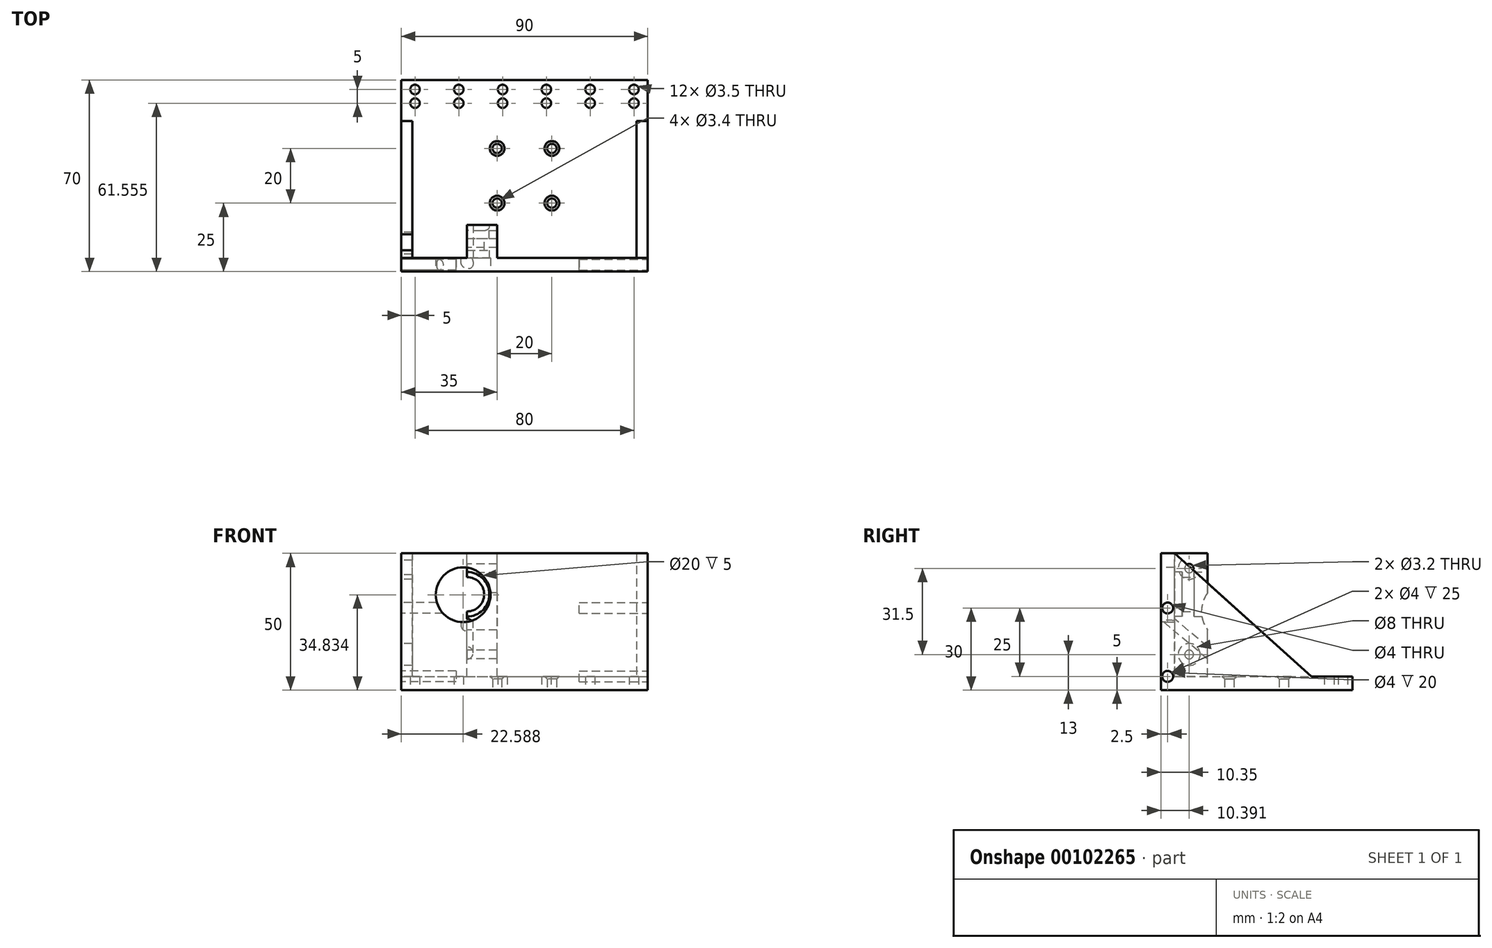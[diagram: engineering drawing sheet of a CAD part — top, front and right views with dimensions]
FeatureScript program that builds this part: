
annotation { "Feature Type Name" : "Feature", "Feature Type Description" : "" }
export const myFeature = defineFeature(function(context is Context, id is Id, definition is map)
    precondition{}
    {
        {
            var Q0;
            Q0=qCreatedBy(makeId("Top.planeOp"),FACE);
            var sketch = newSketch(context, id + "F0", { "sketchPlane" : qUnion([Q0])});
            skLineSegment(sketch, "E0.bottom", {"start": v(0, 0) * mm, "end": v(90, 0) * mm});
            skLineSegment(sketch, "E0.top", {"start": v(0, 70) * mm, "end": v(90, 70) * mm});
            skLineSegment(sketch, "E0.right", {"start": v(90, 0) * mm, "end": v(90, 70) * mm});
            skLineSegment(sketch, "E1", {"start": v(0, 35) * mm, "end": v(98.43, 35) * mm, "construction": true});
            skPoint(sketch, "E1.endSnap0", {"position": v(90, 35) * mm});
            skLineSegment(sketch, "E2", {"start": v(45, 70) * mm, "end": v(45, -10.85) * mm, "construction": true});
            skCircle(sketch, "E3", {"center": v(55, 45) * mm, "radius": 1.7 * mm});
            skCircle(sketch, "E4", {"center": v(55, 25) * mm, "radius": 1.7 * mm});
            skCircle(sketch, "E5", {"center": v(35, 45) * mm, "radius": 1.7 * mm});
            skCircle(sketch, "E6", {"center": v(35, 25) * mm, "radius": 1.7 * mm});
            skCircle(sketch, "E7", {"center": v(5, 66.55) * mm, "radius": 1.75 * mm});
            skCircle(sketch, "E8", {"center": v(5, 61.55) * mm, "radius": 1.75 * mm});
            skCircle(sketch, "E9.1.0.0", {"center": v(21, 66.55) * mm, "radius": 1.75 * mm});
            skCircle(sketch, "E9.1.0.1", {"center": v(21, 61.55) * mm, "radius": 1.75 * mm});
            skCircle(sketch, "E9.2.0.0", {"center": v(37, 66.55) * mm, "radius": 1.75 * mm});
            skCircle(sketch, "E9.2.0.1", {"center": v(37, 61.55) * mm, "radius": 1.75 * mm});
            skCircle(sketch, "E9.3.0.0", {"center": v(53, 66.55) * mm, "radius": 1.75 * mm});
            skCircle(sketch, "E9.3.0.1", {"center": v(53, 61.55) * mm, "radius": 1.75 * mm});
            skCircle(sketch, "E9.4.0.0", {"center": v(69, 66.55) * mm, "radius": 1.75 * mm});
            skCircle(sketch, "E9.4.0.1", {"center": v(69, 61.55) * mm, "radius": 1.75 * mm});
            skCircle(sketch, "E9.5.0.0", {"center": v(85, 66.55) * mm, "radius": 1.75 * mm});
            skCircle(sketch, "E9.5.0.1", {"center": v(85, 61.55) * mm, "radius": 1.75 * mm});
            skLineSegment(sketch, "E9.direction1", {"start": v(5, 66.55) * mm, "end": v(21, 66.55) * mm, "construction": true});
            skLineSegment(sketch, "E10", {"start": v(0, 70) * mm, "end": v(0, 0) * mm});
            skSolve(sketch);
        }
        {
            var Q0;
            Q0 = qSketchRegion(id + "F0", true);
            extrude(context, id + "F1", {"entities" : qUnion([Q0]), "depth" : 5 * mm});
        }
        {
            var Q0;
            Q0=makeQuery(id+"F1.opExtrude","CAP_FACE",FACE,{"disambiguationData":[OSD([sQuery(id+"F0.wireOp",EDGE,"E0.bottom"),sQuery(id+"F0.wireOp",EDGE,"E0.top"),sQuery(id+"F0.wireOp",EDGE,"E0.right"),sQuery(id+"F0.wireOp",EDGE,"E3"),sQuery(id+"F0.wireOp",EDGE,"E4"),sQuery(id+"F0.wireOp",EDGE,"E5"),sQuery(id+"F0.wireOp",EDGE,"E6"),sQuery(id+"F0.wireOp",EDGE,"E7"),sQuery(id+"F0.wireOp",EDGE,"E8"),sQuery(id+"F0.wireOp",EDGE,"E9.1.0.0"),sQuery(id+"F0.wireOp",EDGE,"E9.1.0.1"),sQuery(id+"F0.wireOp",EDGE,"E9.2.0.0"),sQuery(id+"F0.wireOp",EDGE,"E9.2.0.1"),sQuery(id+"F0.wireOp",EDGE,"E9.3.0.0"),sQuery(id+"F0.wireOp",EDGE,"E9.3.0.1"),sQuery(id+"F0.wireOp",EDGE,"E9.4.0.0"),sQuery(id+"F0.wireOp",EDGE,"E9.4.0.1"),sQuery(id+"F0.wireOp",EDGE,"E9.5.0.0"),sQuery(id+"F0.wireOp",EDGE,"E9.5.0.1"),sQuery(id+"F0.wireOp",EDGE,"E10")])],"isStart":false});
            var sketch = newSketch(context, id + "F2", { "sketchPlane" : qUnion([Q0])});
            skLineSegment(sketch, "E11.bottom", {"start": v(0, 0) * mm, "end": v(90, 0) * mm});
            skLineSegment(sketch, "E11.top", {"start": v(0, 5) * mm, "end": v(90, 5) * mm});
            skLineSegment(sketch, "E11.left", {"start": v(0, 0) * mm, "end": v(0, 5) * mm});
            skLineSegment(sketch, "E11.right", {"start": v(90, 0) * mm, "end": v(90, 5) * mm});
            skSolve(sketch);
        }
        {
            var Q0;
            Q0 = qSketchRegion(id + "F2", true);
            extrude(context, id + "F3", {"entities" : qUnion([Q0]), "operationType" : NewBodyOperationType.ADD, "depth" : 45 * mm});
        }
        {
            var Q0;
            Q0=makeQuery(id+"F3.opExtrude","SWEPT_FACE",FACE,{"disambiguationData":[OSD([sQuery(id+"F2.wireOp",EDGE,"E11.top")])]});
            var sketch = newSketch(context, id + "F4", { "sketchPlane" : qUnion([Q0])});
            skLineSegment(sketch, "E12.bottom", {"start": v(-35, 5) * mm, "end": v(-24, 5) * mm});
            skLineSegment(sketch, "E12.top", {"start": v(-35, 50) * mm, "end": v(-24, 50) * mm});
            skLineSegment(sketch, "E12.left", {"start": v(-35, 5) * mm, "end": v(-35, 50) * mm});
            skLineSegment(sketch, "E12.right", {"start": v(-24, 5) * mm, "end": v(-24, 50) * mm});
            skSolve(sketch);
        }
        {
            var Q0;
            Q0 = qSketchRegion(id + "F4", true);
            extrude(context, id + "F5", {"entities" : qUnion([Q0]), "operationType" : NewBodyOperationType.ADD, "depth" : 12.1 * mm});
        }
        {
            var Q0;
            Q0=makeQuery(id+"F5.opExtrude","CAP_FACE",FACE,{"disambiguationData":[OSD([sQuery(id+"F4.wireOp",EDGE,"E12.bottom"),sQuery(id+"F4.wireOp",EDGE,"E12.top"),sQuery(id+"F4.wireOp",EDGE,"E12.left"),sQuery(id+"F4.wireOp",EDGE,"E12.right")])],"isStart":false});
            var sketch = newSketch(context, id + "F6", { "sketchPlane" : qUnion([Q0])});
            skCircle(sketch, "E13", {"center": v(-24, 35) * mm, "radius": 6.25 * mm});
            skSolve(sketch);
        }
        {
            var Q0;
            Q0 = qSketchRegion(id + "F6", true);
            extrude(context, id + "F7", {"entities" : qUnion([Q0]), "operationType" : NewBodyOperationType.REMOVE, "oppositeDirection" : true, "depth" : 25 * mm});
        }
        {
            var Q0;
            Q0=makeQuery(id+"F5.opExtrude","CAP_FACE",FACE,{"disambiguationData":[OSD([sQuery(id+"F4.wireOp",EDGE,"E12.bottom"),sQuery(id+"F4.wireOp",EDGE,"E12.top"),sQuery(id+"F4.wireOp",EDGE,"E12.left"),sQuery(id+"F4.wireOp",EDGE,"E12.right")])],"isStart":false});
            var sketch = newSketch(context, id + "F8", { "sketchPlane" : qUnion([Q0])});
            skCircle(sketch, "E14", {"center": v(-24, 35) * mm, "radius": 8.15 * mm});
            skSolve(sketch);
        }
        {
            var Q0;
            Q0 = qSketchRegion(id + "F8", true);
            extrude(context, id + "F9", {"entities" : qUnion([Q0]), "operationType" : NewBodyOperationType.REMOVE, "oppositeDirection" : true, "depth" : 5 * mm});
        }
        {
            var Q0;
            Q0=makeQuery(id+"F3.boolean.opBoolean","MERGE",FACE,{"derivedFrom":[makeQuery(id+"F1.opExtrude","SWEPT_FACE",FACE,{"disambiguationData":[OSD([sQuery(id+"F0.wireOp",EDGE,"E0.bottom")])]}),makeQuery(id+"F3.opExtrude","SWEPT_FACE",FACE,{"disambiguationData":[OSD([sQuery(id+"F2.wireOp",EDGE,"E11.bottom")])]})]});
            var sketch = newSketch(context, id + "F10", { "sketchPlane" : qUnion([Q0])});
            skCircle(sketch, "E15", {"center": v(22.59, 34.83) * mm, "radius": 10 * mm});
            skSolve(sketch);
        }
        {
            var Q0;
            Q0 = qSketchRegion(id + "F10", true);
            extrude(context, id + "F11", {"entities" : qUnion([Q0]), "operationType" : NewBodyOperationType.REMOVE, "oppositeDirection" : true, "depth" : 5 * mm});
        }
        {
            var Q0;
            Q0=makeQuery(id+"F11.boolean.opBoolean","COPY",FACE,{"derivedFrom":makeQuery(id+"F11.opExtrude","CAP_FACE",FACE,{"disambiguationData":[OSD([sQuery(id+"F10.wireOp",EDGE,"E15")])],"isStart":false})});
            var sketch = newSketch(context, id + "F12", { "sketchPlane" : qUnion([Q0])});
            skCircle(sketch, "E16", {"center": v(24, 35) * mm, "radius": 8.15 * mm});
            skSolve(sketch);
        }
        {
            var Q0;
            Q0 = qSketchRegion(id + "F12", true);
            extrude(context, id + "F13", {"entities" : qUnion([Q0]), "operationType" : NewBodyOperationType.REMOVE, "oppositeDirection" : true, "depth" : 2.8 * mm});
        }
        {
            var Q0;
            {var subQ0=sQuery(id+"F4.wireOp",EDGE,"E12.right");Q0=makeQuery(id+"F7.boolean.opBoolean","SPLIT",FACE,{"disambiguationData":[TD([makeQuery(id+"F1.opExtrude","CAP_FACE",FACE,{"disambiguationData":[OSD([sQuery(id+"F0.wireOp",EDGE,"E0.bottom"),sQuery(id+"F0.wireOp",EDGE,"E0.top"),sQuery(id+"F0.wireOp",EDGE,"E0.right"),sQuery(id+"F0.wireOp",EDGE,"E3"),sQuery(id+"F0.wireOp",EDGE,"E4"),sQuery(id+"F0.wireOp",EDGE,"E5"),sQuery(id+"F0.wireOp",EDGE,"E6"),sQuery(id+"F0.wireOp",EDGE,"E7"),sQuery(id+"F0.wireOp",EDGE,"E8"),sQuery(id+"F0.wireOp",EDGE,"E9.1.0.0"),sQuery(id+"F0.wireOp",EDGE,"E9.1.0.1"),sQuery(id+"F0.wireOp",EDGE,"E9.2.0.0"),sQuery(id+"F0.wireOp",EDGE,"E9.2.0.1"),sQuery(id+"F0.wireOp",EDGE,"E9.3.0.0"),sQuery(id+"F0.wireOp",EDGE,"E9.3.0.1"),sQuery(id+"F0.wireOp",EDGE,"E9.4.0.0"),sQuery(id+"F0.wireOp",EDGE,"E9.4.0.1"),sQuery(id+"F0.wireOp",EDGE,"E9.5.0.0"),sQuery(id+"F0.wireOp",EDGE,"E9.5.0.1"),sQuery(id+"F0.wireOp",EDGE,"E10")])],"isStart":false})])],"derivedFrom":makeQuery(id+"F5.opExtrude","SWEPT_FACE",FACE,{"disambiguationData":[OSD([subQ0])]})});}
            var sketch = newSketch(context, id + "F14", { "sketchPlane" : qUnion([Q0])});
            skCircle(sketch, "E17", {"center": v(-10.35, 44.5) * mm, "radius": 1.6 * mm});
            skCircle(sketch, "E18", {"center": v(-10.35, 13) * mm, "radius": 1.6 * mm});
            skCircle(sketch, "E19", {"center": v(-26.1, 28.75) * mm, "radius": 11.25 * mm});
            skSolve(sketch);
        }
        {
            var Q0;
            Q0 = qSketchRegion(id + "F14", true);
            extrude(context, id + "F15", {"entities" : qUnion([Q0]), "operationType" : NewBodyOperationType.REMOVE, "oppositeDirection" : true, "depth" : 25 * mm});
        }
        {
            var Q0;
            Q0=makeQuery(id+"F3.boolean.opBoolean","MERGE",FACE,{"derivedFrom":[makeQuery(id+"F1.opExtrude","SWEPT_FACE",FACE,{"disambiguationData":[OSD([sQuery(id+"F0.wireOp",EDGE,"E10")])]}),makeQuery(id+"F3.opExtrude","SWEPT_FACE",FACE,{"disambiguationData":[OSD([sQuery(id+"F2.wireOp",EDGE,"E11.left")])]})]});
            var sketch = newSketch(context, id + "F16", { "sketchPlane" : qUnion([Q0])});
            skLineSegment(sketch, "E20", {"start": v(-5, 50) * mm, "end": v(-55, 5) * mm});
            skLineSegment(sketch, "E21", {"start": v(-55, 5) * mm, "end": v(-55, 0) * mm});
            skLineSegment(sketch, "E22", {"start": v(-55, 0) * mm, "end": v(0, 0) * mm});
            skLineSegment(sketch, "E23", {"start": v(0, 0) * mm, "end": v(0, 50) * mm});
            skLineSegment(sketch, "E24", {"start": v(0, 50) * mm, "end": v(-5, 50) * mm});
            skSolve(sketch);
        }
        {
            var Q0;
            Q0 = qSketchRegion(id + "F16", true);
            extrude(context, id + "F17", {"entities" : qUnion([Q0]), "operationType" : NewBodyOperationType.ADD, "oppositeDirection" : true, "depth" : 4 * mm});
        }
        {
            var Q0;
            Q0=makeQuery(id+"F3.boolean.opBoolean","MERGE",FACE,{"derivedFrom":[makeQuery(id+"F1.opExtrude","SWEPT_FACE",FACE,{"disambiguationData":[OSD([sQuery(id+"F0.wireOp",EDGE,"E0.right")])]}),makeQuery(id+"F3.opExtrude","SWEPT_FACE",FACE,{"disambiguationData":[OSD([sQuery(id+"F2.wireOp",EDGE,"E11.right")])]})]});
            var sketch = newSketch(context, id + "F18", { "sketchPlane" : qUnion([Q0])});
            skLineSegment(sketch, "E25", {"start": v(5, 50) * mm, "end": v(55, 5) * mm});
            skLineSegment(sketch, "E26", {"start": v(55, 5) * mm, "end": v(55, 0) * mm});
            skLineSegment(sketch, "E27", {"start": v(55, 0) * mm, "end": v(0, 0) * mm});
            skLineSegment(sketch, "E28", {"start": v(0, 0) * mm, "end": v(0, 50) * mm});
            skLineSegment(sketch, "E29", {"start": v(0, 50) * mm, "end": v(5, 50) * mm});
            skSolve(sketch);
        }
        {
            var Q0;
            Q0 = qSketchRegion(id + "F18", true);
            extrude(context, id + "F19", {"entities" : qUnion([Q0]), "operationType" : NewBodyOperationType.ADD, "oppositeDirection" : true, "depth" : 4 * mm});
        }
        {
            var Q0;
            Q0=makeQuery(id+"F17.boolean.opBoolean","MERGE",FACE,{"derivedFrom":[makeQuery(id+"F3.boolean.opBoolean","MERGE",FACE,{"derivedFrom":[makeQuery(id+"F1.opExtrude","SWEPT_FACE",FACE,{"disambiguationData":[OSD([sQuery(id+"F0.wireOp",EDGE,"E10")])]}),makeQuery(id+"F3.opExtrude","SWEPT_FACE",FACE,{"disambiguationData":[OSD([sQuery(id+"F2.wireOp",EDGE,"E11.left")])]})]}),makeQuery(id+"F17.opExtrude","CAP_FACE",FACE,{"disambiguationData":[OSD([sQuery(id+"F16.wireOp",EDGE,"E20"),sQuery(id+"F16.wireOp",EDGE,"E21"),sQuery(id+"F16.wireOp",EDGE,"E22"),sQuery(id+"F16.wireOp",EDGE,"E23"),sQuery(id+"F16.wireOp",EDGE,"E24")])],"isStart":true})]});
            var sketch = newSketch(context, id + "F20", { "sketchPlane" : qUnion([Q0])});
            skCircle(sketch, "E30", {"center": v(-10.4, 44.5) * mm, "radius": 4 * mm});
            skCircle(sketch, "E31", {"center": v(-10.4, 13) * mm, "radius": 4 * mm});
            skSolve(sketch);
        }
        {
            var Q0;
            Q0 = qSketchRegion(id + "F20", true);
            extrude(context, id + "F21", {"entities" : qUnion([Q0]), "operationType" : NewBodyOperationType.REMOVE, "oppositeDirection" : true, "depth" : 5 * mm});
        }
        {
            var Q0;
            Q0=makeQuery(id+"F17.boolean.opBoolean","MERGE",FACE,{"derivedFrom":[makeQuery(id+"F3.boolean.opBoolean","MERGE",FACE,{"derivedFrom":[makeQuery(id+"F1.opExtrude","SWEPT_FACE",FACE,{"disambiguationData":[OSD([sQuery(id+"F0.wireOp",EDGE,"E10")])]}),makeQuery(id+"F3.opExtrude","SWEPT_FACE",FACE,{"disambiguationData":[OSD([sQuery(id+"F2.wireOp",EDGE,"E11.left")])]})]}),makeQuery(id+"F17.opExtrude","CAP_FACE",FACE,{"disambiguationData":[OSD([sQuery(id+"F16.wireOp",EDGE,"E20"),sQuery(id+"F16.wireOp",EDGE,"E21"),sQuery(id+"F16.wireOp",EDGE,"E22"),sQuery(id+"F16.wireOp",EDGE,"E23"),sQuery(id+"F16.wireOp",EDGE,"E24")])],"isStart":true})]});
            var sketch = newSketch(context, id + "F22", { "sketchPlane" : qUnion([Q0])});
            skCircle(sketch, "E32", {"center": v(-2.5, 5) * mm, "radius": 2 * mm});
            skCircle(sketch, "E33", {"center": v(-2.5, 30) * mm, "radius": 2 * mm});
            skSolve(sketch);
        }
        {
            var Q0;
            Q0 = qSketchRegion(id + "F22", true);
            extrude(context, id + "F23", {"entities" : qUnion([Q0]), "operationType" : NewBodyOperationType.REMOVE, "oppositeDirection" : true, "depth" : 20 * mm});
        }
        {
            var Q0;
            Q0=makeQuery(id+"F1.opExtrude","CAP_EDGE",EDGE,{"disambiguationData":[OSD([sQuery(id+"F0.wireOp",EDGE,"E5")])],"isStart":false});
            var Q1;
            Q1=makeQuery(id+"F1.opExtrude","CAP_EDGE",EDGE,{"disambiguationData":[OSD([sQuery(id+"F0.wireOp",EDGE,"E3")])],"isStart":false});
            var Q2;
            Q2=makeQuery(id+"F1.opExtrude","CAP_EDGE",EDGE,{"disambiguationData":[OSD([sQuery(id+"F0.wireOp",EDGE,"E4")])],"isStart":false});
            var Q3;
            Q3=makeQuery(id+"F1.opExtrude","CAP_EDGE",EDGE,{"disambiguationData":[OSD([sQuery(id+"F0.wireOp",EDGE,"E6")])],"isStart":false});
            chamfer(context, id + "F24", {"entities" : qUnion([Q0, Q1, Q2, Q3]), "width" : 1 * mm, "tangentPropagation" : true});
        }
        {
            var Q0;
            {var subQ0=sQuery(id+"F4.wireOp",EDGE,"E12.right");Q0=makeQuery(id+"F7.boolean.opBoolean","SPLIT",FACE,{"disambiguationData":[TD([makeQuery(id+"F1.opExtrude","CAP_FACE",FACE,{"disambiguationData":[OSD([sQuery(id+"F0.wireOp",EDGE,"E0.bottom"),sQuery(id+"F0.wireOp",EDGE,"E0.top"),sQuery(id+"F0.wireOp",EDGE,"E0.right"),sQuery(id+"F0.wireOp",EDGE,"E3"),sQuery(id+"F0.wireOp",EDGE,"E4"),sQuery(id+"F0.wireOp",EDGE,"E5"),sQuery(id+"F0.wireOp",EDGE,"E6"),sQuery(id+"F0.wireOp",EDGE,"E7"),sQuery(id+"F0.wireOp",EDGE,"E8"),sQuery(id+"F0.wireOp",EDGE,"E9.1.0.0"),sQuery(id+"F0.wireOp",EDGE,"E9.1.0.1"),sQuery(id+"F0.wireOp",EDGE,"E9.2.0.0"),sQuery(id+"F0.wireOp",EDGE,"E9.2.0.1"),sQuery(id+"F0.wireOp",EDGE,"E9.3.0.0"),sQuery(id+"F0.wireOp",EDGE,"E9.3.0.1"),sQuery(id+"F0.wireOp",EDGE,"E9.4.0.0"),sQuery(id+"F0.wireOp",EDGE,"E9.4.0.1"),sQuery(id+"F0.wireOp",EDGE,"E9.5.0.0"),sQuery(id+"F0.wireOp",EDGE,"E9.5.0.1"),sQuery(id+"F0.wireOp",EDGE,"E10")])],"isStart":false})])],"derivedFrom":makeQuery(id+"F5.opExtrude","SWEPT_FACE",FACE,{"disambiguationData":[OSD([subQ0])]})});}
            var sketch = newSketch(context, id + "F25", { "sketchPlane" : qUnion([Q0])});
            skLineSegment(sketch, "E34", {"start": v(1.5, 28.5) * mm, "end": v(-22.1, 8.5) * mm});
            skSolve(sketch);
        }
        {
            var Q0;
            Q0=makeQuery(id+"F3.boolean.opBoolean","MERGE",FACE,{"derivedFrom":[makeQuery(id+"F1.opExtrude","SWEPT_FACE",FACE,{"disambiguationData":[OSD([sQuery(id+"F0.wireOp",EDGE,"E0.bottom")])]}),makeQuery(id+"F3.opExtrude","SWEPT_FACE",FACE,{"disambiguationData":[OSD([sQuery(id+"F2.wireOp",EDGE,"E11.bottom")])]})]});
            var sketch = newSketch(context, id + "F26", { "sketchPlane" : qUnion([Q0])});
            skCircle(sketch, "E35", {"center": v(23.99, 28.05) * mm, "radius": 2.25 * mm});
            skSolve(sketch);
        }
        {
            var Q0;
            Q0 = qSketchRegion(id + "F26", true);
            var Q1;
            Q1=sQuery(id+"F25.wireOp",EDGE,"E34");
            sweep(context, id + "F27", {"operationType" : NewBodyOperationType.REMOVE, "profiles" : qUnion([Q0]), "path" : qUnion([Q1])});
        }
        {
            var Q0;
            Q0=makeQuery(id+"F19.boolean.opBoolean","MERGE",FACE,{"derivedFrom":[makeQuery(id+"F3.boolean.opBoolean","MERGE",FACE,{"derivedFrom":[makeQuery(id+"F1.opExtrude","SWEPT_FACE",FACE,{"disambiguationData":[OSD([sQuery(id+"F0.wireOp",EDGE,"E0.right")])]}),makeQuery(id+"F3.opExtrude","SWEPT_FACE",FACE,{"disambiguationData":[OSD([sQuery(id+"F2.wireOp",EDGE,"E11.right")])]})]}),makeQuery(id+"F19.opExtrude","CAP_FACE",FACE,{"disambiguationData":[OSD([sQuery(id+"F18.wireOp",EDGE,"E25"),sQuery(id+"F18.wireOp",EDGE,"E26"),sQuery(id+"F18.wireOp",EDGE,"E27"),sQuery(id+"F18.wireOp",EDGE,"E28"),sQuery(id+"F18.wireOp",EDGE,"E29")])],"isStart":true})]});
            var sketch = newSketch(context, id + "F28", { "sketchPlane" : qUnion([Q0])});
            skCircle(sketch, "E36", {"center": v(2.5, 5) * mm, "radius": 2 * mm});
            skCircle(sketch, "E37", {"center": v(2.5, 30) * mm, "radius": 2 * mm});
            skSolve(sketch);
        }
        {
            var Q0;
            Q0 = qSketchRegion(id + "F28", true);
            extrude(context, id + "F29", {"entities" : qUnion([Q0]), "operationType" : NewBodyOperationType.REMOVE, "oppositeDirection" : true, "depth" : 25 * mm});
        }
    });
